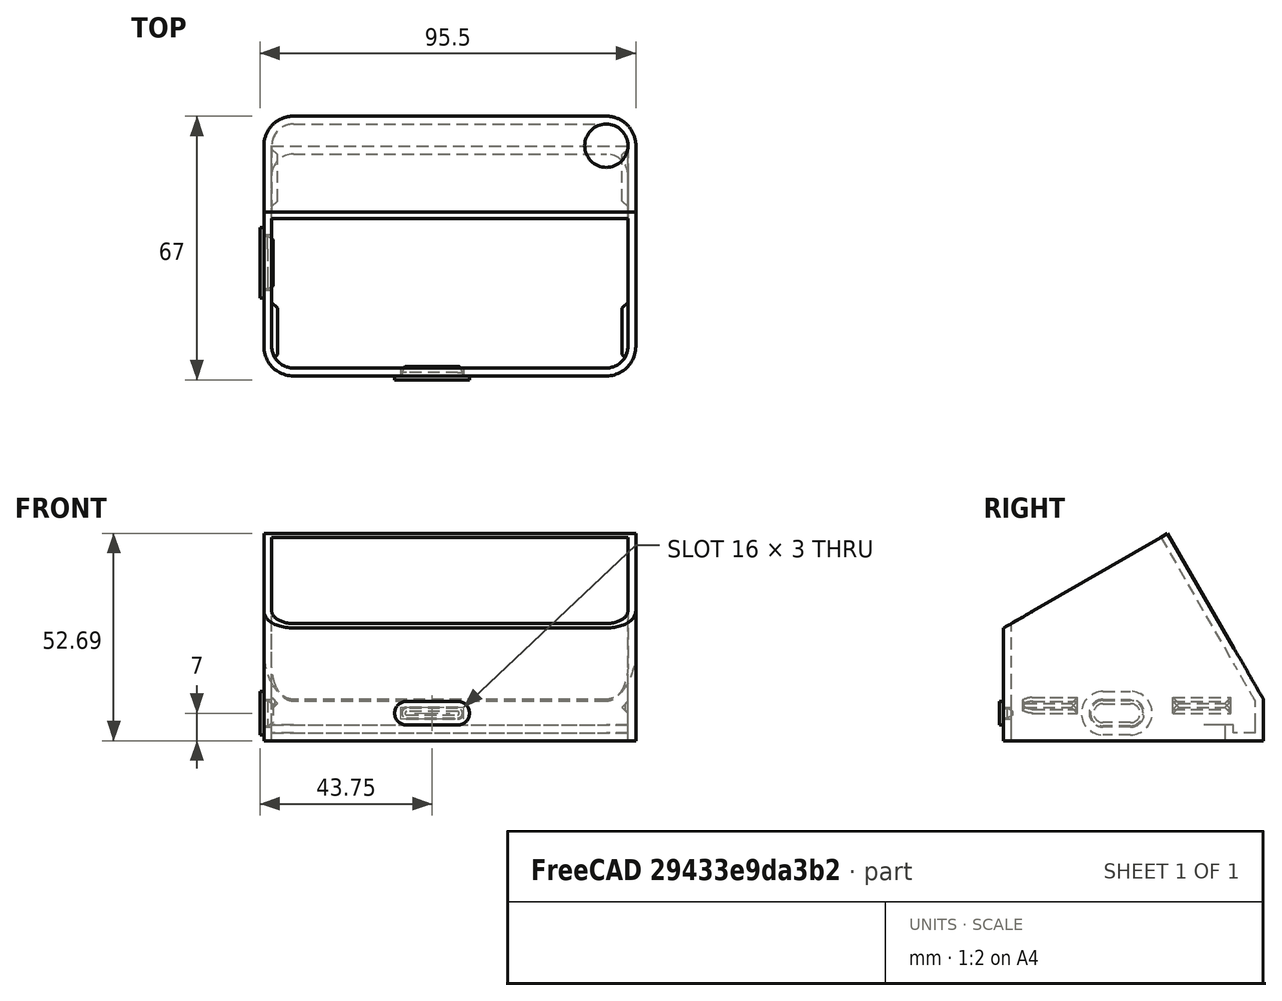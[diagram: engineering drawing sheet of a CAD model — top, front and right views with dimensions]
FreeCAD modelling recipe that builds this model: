
FCSTD DOCUMENT  (FreeCAD 0.21R33771 (Git))
Label: 2432S028
License: All rights reserved
LicenseURL: http://en.wikipedia.org/wiki/All_rights_reserved
objects: Sketcher::SketchObject×12, Part::Extrusion×11, Part::Box×7, Part::Chamfer×6, Part::Cut×4, Part::FeaturePython×3, Mesh::Feature×3, Part::MultiCommon×1, Part::MultiFuse×1
note: 45 computed .brp shape members not serialized (recipe doc carries the construction recipe); baked Part::Feature solids carry a one-line shape summary decoded from their .brp

FEATURE [Sketcher::SketchObject] Sketch  label="Basis"
  FullyConstrained = true
  sketch-geometry (22):
    g0: LineSegment StartX=-39.75 StartY=33 StartZ=0 EndX=39.75 EndY=33 EndZ=0
    g1: LineSegment StartX=47.25 StartY=25.5 StartZ=0 EndX=47.25 EndY=-25.5 EndZ=0
    g2: LineSegment StartX=39.75 StartY=-33 StartZ=0 EndX=-39.75 EndY=-33 EndZ=0
    g3: LineSegment StartX=-47.25 StartY=-25.5 StartZ=0 EndX=-47.25 EndY=25.5 EndZ=0
    g4: ArcOfCircle CenterX=-39.75 CenterY=25.5 CenterZ=0 NormalX=0 NormalY=0 NormalZ=1 AngleXU=0 Radius=7.5 StartAngle=1.5708 EndAngle=3.14159
    g5: GeomPoint X=-47.25 Y=33 Z=0
    g6: ArcOfCircle CenterX=39.75 CenterY=25.5 CenterZ=0 NormalX=0 NormalY=0 NormalZ=1 AngleXU=0 Radius=7.5 StartAngle=0 EndAngle=1.5708
    g7: GeomPoint X=47.25 Y=33 Z=0
    g8: ArcOfCircle CenterX=39.75 CenterY=-25.5 CenterZ=0 NormalX=0 NormalY=0 NormalZ=1 AngleXU=0 Radius=7.5 StartAngle=4.71239 EndAngle=6.28319
    g9: GeomPoint X=47.25 Y=-33 Z=0
    g10: ArcOfCircle CenterX=-39.75 CenterY=-25.5 CenterZ=0 NormalX=0 NormalY=0 NormalZ=1 AngleXU=0 Radius=7.5 StartAngle=3.14159 EndAngle=4.71239
    g11: GeomPoint X=-47.25 Y=-33 Z=0
    g12: ArcOfCircle CenterX=39.75 CenterY=17.9 CenterZ=0 NormalX=0 NormalY=0 NormalZ=1 AngleXU=0 Radius=5.5 StartAngle=4e-16 EndAngle=1.5708
    g13: LineSegment StartX=45.25 StartY=17.9 StartZ=0 EndX=45.25 EndY=-25.5 EndZ=0
    g14: ArcOfCircle CenterX=39.75 CenterY=-25.5 CenterZ=0 NormalX=0 NormalY=0 NormalZ=1 AngleXU=0 Radius=5.5 StartAngle=4.71239 EndAngle=6.28319
    g15: LineSegment StartX=39.75 StartY=-31 StartZ=0 EndX=-39.75 EndY=-31 EndZ=0
    g16: ArcOfCircle CenterX=-39.75 CenterY=-25.5 CenterZ=0 NormalX=0 NormalY=0 NormalZ=1 AngleXU=0 Radius=5.5 StartAngle=3.14159 EndAngle=4.71239
    g17: LineSegment StartX=-45.25 StartY=-25.5 StartZ=0 EndX=-45.25 EndY=17.9 EndZ=0
    g18: ArcOfCircle CenterX=-39.75 CenterY=17.9 CenterZ=0 NormalX=0 NormalY=0 NormalZ=1 AngleXU=0 Radius=5.5 StartAngle=1.5708 EndAngle=3.14159
    g19: LineSegment StartX=-39.75 StartY=23.4 StartZ=0 EndX=39.75 EndY=23.4 EndZ=0
    g20: GeomPoint X=45.25 Y=23.4 Z=0
    g21: GeomPoint X=-45.25 Y=-31 Z=0
  constraints (50):
    c: Horizontal(g0)
    c: Horizontal(g2)
    c: Vertical(g1)
    c: Vertical(g3)
    c: DistanceY(g9,g7) = 66
    c: Symmetric(g5,g9,g-1)
    c: PointOnObject(g5,g0)
    c: PointOnObject(g5,g3)
    c: Tangent(g0,g4) = 1.5708
    c: Tangent(g3,g4) = 1.5708
    c: PointOnObject(g7,g0)
    c: PointOnObject(g7,g1)
    c: Tangent(g0,g6) = 1.5708
    c: Tangent(g1,g6) = 1.5708
    c: PointOnObject(g9,g1)
    c: PointOnObject(g9,g2)
    c: Tangent(g1,g8) = 1.5708
    c: Tangent(g2,g8) = 1.5708
    c: PointOnObject(g11,g2)
    c: PointOnObject(g11,g3)
    c: Tangent(g2,g10) = 1.5708
    c: Tangent(g3,g10) = 1.5708
    c: Equal(g8,g10)
    c: Equal(g10,g4)
    c: Equal(g4,g6)
    c: Tangent(g12,g13) = 1.5708
    c: Tangent(g13,g14) = 1.5708
    c: Tangent(g14,g15) = 1.5708
    c: Tangent(g15,g16) = 1.5708
    c: Tangent(g16,g17) = 1.5708
    c: Tangent(g17,g18) = 1.5708
    c: Tangent(g18,g19) = 1.5708
    c: Tangent(g19,g12) = 1.5708
    c: Horizontal(g15)
    c: Vertical(g13)
    c: Vertical(g17)
    c: Equal(g12,g14)
    c: Equal(g14,g16)
    c: Equal(g16,g18)
    c: PointOnObject(g20,g13)
    c: PointOnObject(g20,g19)
    c: PointOnObject(g21,g15)
    c: PointOnObject(g21,g17)
    c: DistanceY(g14,g12) = 54.4
    c: DistanceX(g17,g12) = 90.5
    c: Diameter(g12) = 11
    c: Symmetric(g12,g17,g-2)
    c: DistanceY(g2,g14) = 2
    c: Coincident(g10,g16)
    c: DistanceY(g18,g4) = 2.1
FEATURE [Part::Box] Box  label="Cube"
  AttacherType = Attacher::AttachEngine3D
  Height = 100
  Length = 100
  Placement = pos=(-50,39.3072,-0.4) rot=(1,0,0;0.523599rad)
  Width = 100
FEATURE [Sketcher::SketchObject] Sketch001
  ExternalGeometry = -> [Sketch]
  FullyConstrained = true
  sketch-geometry (20):
    g0: ArcOfCircle CenterX=-39.75 CenterY=25.5 CenterZ=0 NormalX=0 NormalY=0 NormalZ=1 AngleXU=0 Radius=7.5 StartAngle=1.5708 EndAngle=3.14159
    g1: LineSegment StartX=-39.75 StartY=33 StartZ=0 EndX=39.75 EndY=33 EndZ=0
    g2: ArcOfCircle CenterX=39.75 CenterY=25.5 CenterZ=0 NormalX=0 NormalY=0 NormalZ=1 AngleXU=0 Radius=7.5 StartAngle=1e-16 EndAngle=1.5708
    g3: LineSegment StartX=47.25 StartY=25.5 StartZ=0 EndX=47.25 EndY=-25.5 EndZ=0
    g4: ArcOfCircle CenterX=39.75 CenterY=-25.5 CenterZ=0 NormalX=0 NormalY=0 NormalZ=1 AngleXU=0 Radius=7.5 StartAngle=4.71239 EndAngle=6.28319
    g5: LineSegment StartX=39.75 StartY=-33 StartZ=0 EndX=-39.75 EndY=-33 EndZ=0
    g6: ArcOfCircle CenterX=-39.75 CenterY=-25.5 CenterZ=0 NormalX=0 NormalY=0 NormalZ=1 AngleXU=0 Radius=7.5 StartAngle=3.14159 EndAngle=4.71239
    g7: LineSegment StartX=-47.25 StartY=-25.5 StartZ=0 EndX=-47.25 EndY=25.5 EndZ=0
    g8: GeomPoint X=-47.25 Y=33 Z=0
    g9: GeomPoint X=47.25 Y=-33 Z=0
    g10: ArcOfCircle CenterX=-39.75 CenterY=17.9 CenterZ=0 NormalX=0 NormalY=0 NormalZ=1 AngleXU=0 Radius=5.5 StartAngle=1.5708 EndAngle=3.14159
    g11: LineSegment StartX=-39.75 StartY=23.4 StartZ=0 EndX=39.75 EndY=23.4 EndZ=0
    g12: ArcOfCircle CenterX=39.75 CenterY=17.9 CenterZ=0 NormalX=0 NormalY=0 NormalZ=1 AngleXU=0 Radius=5.5 StartAngle=0 EndAngle=1.5708
    g13: LineSegment StartX=45.25 StartY=17.9 StartZ=0 EndX=45.25 EndY=-25.5 EndZ=0
    g14: ArcOfCircle CenterX=39.75 CenterY=-25.5 CenterZ=0 NormalX=0 NormalY=0 NormalZ=1 AngleXU=0 Radius=5.5 StartAngle=4.71239 EndAngle=6.28319
    g15: LineSegment StartX=39.75 StartY=-31 StartZ=0 EndX=-39.75 EndY=-31 EndZ=0
    g16: ArcOfCircle CenterX=-39.75 CenterY=-25.5 CenterZ=0 NormalX=0 NormalY=0 NormalZ=1 AngleXU=0 Radius=5.5 StartAngle=3.14159 EndAngle=4.71239
    g17: LineSegment StartX=-45.25 StartY=-25.5 StartZ=0 EndX=-45.25 EndY=17.9 EndZ=0
    g18: GeomPoint X=-45.25 Y=23.4 Z=0
    g19: GeomPoint X=45.25 Y=-31 Z=0
  constraints (44):
    c: Tangent(g0,g1) = 1.5708
    c: Tangent(g1,g2) = 1.5708
    c: Tangent(g2,g3) = 1.5708
    c: Tangent(g3,g4) = 1.5708
    c: Tangent(g4,g5) = 1.5708
    c: Tangent(g5,g6) = 1.5708
    c: Tangent(g6,g7) = 1.5708
    c: Tangent(g7,g0) = 1.5708
    c: Horizontal(g1)
    c: Horizontal(g5)
    c: Vertical(g3)
    c: Vertical(g7)
    c: Equal(g0,g2)
    c: Equal(g2,g4)
    c: Equal(g4,g6)
    c: PointOnObject(g8,g1)
    c: PointOnObject(g8,g7)
    c: PointOnObject(g9,g3)
    c: PointOnObject(g9,g5)
    c: Coincident(g-6,g4)
    c: Coincident(g0,g-3)
    c: Horizontal(g-3,g0)
    c: Tangent(g10,g11) = 1.5708
    c: Tangent(g11,g12) = 1.5708
    c: Tangent(g12,g13) = 1.5708
    c: Tangent(g13,g14) = 1.5708
    c: Tangent(g14,g15) = 1.5708
    c: Tangent(g15,g16) = 1.5708
    c: Tangent(g16,g17) = 1.5708
    c: Tangent(g17,g10) = 1.5708
    c: Horizontal(g11)
    c: Horizontal(g15)
    c: Vertical(g13)
    c: Vertical(g17)
    c: Equal(g10,g12)
    c: Equal(g12,g14)
    c: Equal(g14,g16)
    c: PointOnObject(g18,g11)
    c: PointOnObject(g18,g17)
    c: PointOnObject(g19,g13)
    c: PointOnObject(g19,g15)
    c: Coincident(g14,g4)
    c: Coincident(g10,g-5)
    c: Horizontal(g-5,g10)
FEATURE [Part::Extrusion] Extrude
  Base = -> Sketch001
  Dir = (0,0,1)
  DirMode = 2
  FaceMakerClass = Part::FaceMakerBullseye
  LengthFwd = 2
  LengthRev = 0
  Solid = true
  Symmetric = false
FEATURE [Sketcher::SketchObject] Sketch002
  ExternalGeometry = -> [Sketch]
  FullyConstrained = true
  Placement = pos=(0,0,2) rot=(0,0,1;0rad)
  sketch-geometry (26):
    g0: ArcOfCircle CenterX=-39.75 CenterY=25.5 CenterZ=0 NormalX=0 NormalY=0 NormalZ=1 AngleXU=0 Radius=7.5 StartAngle=1.5708 EndAngle=3.14159
    g1: LineSegment StartX=-39.75 StartY=33 StartZ=0 EndX=39.75 EndY=33 EndZ=0
    g2: ArcOfCircle CenterX=39.75 CenterY=25.5 CenterZ=0 NormalX=0 NormalY=0 NormalZ=1 AngleXU=0 Radius=7.5 StartAngle=4e-16 EndAngle=1.5708
    g3: LineSegment StartX=47.25 StartY=25.5 StartZ=0 EndX=47.25 EndY=-25.5 EndZ=0
    g4: ArcOfCircle CenterX=39.75 CenterY=-25.5 CenterZ=0 NormalX=0 NormalY=0 NormalZ=1 AngleXU=0 Radius=7.5 StartAngle=4.71239 EndAngle=6.28319
    g5: LineSegment StartX=39.75 StartY=-33 StartZ=0 EndX=-39.75 EndY=-33 EndZ=0
    g6: ArcOfCircle CenterX=-39.75 CenterY=-25.5 CenterZ=0 NormalX=0 NormalY=0 NormalZ=1 AngleXU=0 Radius=7.5 StartAngle=3.14159 EndAngle=4.71239
    g7: LineSegment StartX=-47.25 StartY=-25.5 StartZ=0 EndX=-47.25 EndY=25.5 EndZ=0
    g8: GeomPoint X=-47.25 Y=33 Z=0
    g9: GeomPoint X=47.25 Y=-33 Z=0
    g10: ArcOfCircle CenterX=-39.75 CenterY=17.9 CenterZ=0 NormalX=0 NormalY=0 NormalZ=1 AngleXU=0 Radius=5.5 StartAngle=1.5708 EndAngle=3.14159
    g11: LineSegment StartX=-39.75 StartY=23.4 StartZ=0 EndX=39.75 EndY=23.4 EndZ=0
    g12: ArcOfCircle CenterX=39.75 CenterY=17.9 CenterZ=0 NormalX=0 NormalY=0 NormalZ=1 AngleXU=0 Radius=5.5 StartAngle=0 EndAngle=1.5708
    g13: LineSegment StartX=45.25 StartY=17.9 StartZ=0 EndX=45.25 EndY=-25.5 EndZ=0
    g14: ArcOfCircle CenterX=39.75 CenterY=-25.5 CenterZ=0 NormalX=0 NormalY=0 NormalZ=1 AngleXU=0 Radius=5.5 StartAngle=4.71239 EndAngle=6.28319
    g15: LineSegment StartX=39.75 StartY=-31 StartZ=0 EndX=-39.75 EndY=-31 EndZ=0
    g16: ArcOfCircle CenterX=-39.75 CenterY=-25.5 CenterZ=0 NormalX=0 NormalY=0 NormalZ=1 AngleXU=0 Radius=5.5 StartAngle=3.14159 EndAngle=4.71239
    g17: LineSegment StartX=-45.25 StartY=-25.5 StartZ=0 EndX=-45.25 EndY=17.9 EndZ=0
    g18: GeomPoint X=-45.25 Y=23.4 Z=0
    g19: GeomPoint X=45.25 Y=-31 Z=0
    g20: ArcOfCircle CenterX=-39.75 CenterY=25.5 CenterZ=0 NormalX=0 NormalY=0 NormalZ=1 AngleXU=0 Radius=5.5 StartAngle=1.5708 EndAngle=3.14159
    g21: LineSegment StartX=-39.75 StartY=31 StartZ=0 EndX=39.75 EndY=31 EndZ=0
    g22: ArcOfCircle CenterX=39.75 CenterY=25.5 CenterZ=0 NormalX=0 NormalY=0 NormalZ=1 AngleXU=0 Radius=5.5 StartAngle=0 EndAngle=1.5708
    g23: LineSegment StartX=-45.25 StartY=25.4 StartZ=0 EndX=45.25 EndY=25.4 EndZ=0
    g24: LineSegment StartX=-45.25 StartY=25.5 StartZ=0 EndX=-45.25 EndY=25.4 EndZ=0
    g25: LineSegment StartX=45.25 StartY=25.5 StartZ=0 EndX=45.25 EndY=25.4 EndZ=0
  constraints (62):
    c: Tangent(g0,g1) = 1.5708
    c: Tangent(g1,g2) = 1.5708
    c: Tangent(g2,g3) = 1.5708
    c: Tangent(g3,g4) = 1.5708
    c: Tangent(g4,g5) = 1.5708
    c: Tangent(g5,g6) = 1.5708
    c: Tangent(g6,g7) = 1.5708
    c: Tangent(g7,g0) = 1.5708
    c: Horizontal(g1)
    c: Horizontal(g5)
    c: Vertical(g3)
    c: Vertical(g7)
    c: Equal(g0,g2)
    c: Equal(g2,g4)
    c: Equal(g4,g6)
    c: PointOnObject(g8,g1)
    c: PointOnObject(g8,g7)
    c: PointOnObject(g9,g3)
    c: PointOnObject(g9,g5)
    c: Coincident(g4,g-6)
    c: Coincident(g0,g-3)
    c: Horizontal(g-3,g0)
    c: Tangent(g10,g11) = 1.5708
    c: Tangent(g11,g12) = 1.5708
    c: Tangent(g12,g13) = 1.5708
    c: Tangent(g13,g14) = 1.5708
    c: Tangent(g14,g15) = 1.5708
    c: Tangent(g15,g16) = 1.5708
    c: Tangent(g16,g17) = 1.5708
    c: Tangent(g17,g10) = 1.5708
    c: Horizontal(g11)
    c: Horizontal(g15)
    c: Vertical(g13)
    c: Vertical(g17)
    c: Equal(g10,g12)
    c: Equal(g12,g14)
    c: Equal(g14,g16)
    c: PointOnObject(g18,g11)
    c: PointOnObject(g18,g17)
    c: PointOnObject(g19,g13)
    c: PointOnObject(g19,g15)
    c: Coincident(g4,g14)
    c: Coincident(g10,g-5)
    c: Horizontal(g14,g-6)
    c: Coincident(g20,g0)
    c: Vertical(g0,g20)
    c: Horizontal(g0,g20)
    c: DistanceY(g20,g0) = 2
    c: Coincident(g21,g20)
    c: Horizontal(g21)
    c: Coincident(g22,g2)
    c: Coincident(g22,g21)
    c: Equal(g22,g20)
    c: Horizontal(g2,g22)
    c: Horizontal(g23)
    c: Coincident(g24,g20)
    c: Coincident(g24,g23)
    c: Vertical(g24)
    c: Coincident(g25,g22)
    c: Coincident(g25,g23)
    c: Vertical(g25)
    c: DistanceY(g10,g23) = 2
FEATURE [Part::Extrusion] Extrude001  label="Extrude_2mm"
  Base = -> Sketch002
  Dir = (0,0,1)
  DirMode = 2
  FaceMakerClass = Part::FaceMakerBullseye
  LengthFwd = 2
  LengthRev = 0
  Solid = true
  Symmetric = false
FEATURE [Sketcher::SketchObject] Sketch003
  ExternalGeometry = -> [Sketch]
  FullyConstrained = true
  Placement = pos=(0,0,4) rot=(0,0,1;0rad)
  sketch-geometry (20):
    g0: ArcOfCircle CenterX=-39.75 CenterY=25.5 CenterZ=0 NormalX=0 NormalY=0 NormalZ=1 AngleXU=0 Radius=7.5 StartAngle=1.5708 EndAngle=3.14159
    g1: LineSegment StartX=-39.75 StartY=33 StartZ=0 EndX=39.75 EndY=33 EndZ=0
    g2: ArcOfCircle CenterX=39.75 CenterY=25.5 CenterZ=0 NormalX=0 NormalY=0 NormalZ=1 AngleXU=0 Radius=7.5 StartAngle=0 EndAngle=1.5708
    g3: LineSegment StartX=47.25 StartY=25.5 StartZ=0 EndX=47.25 EndY=-25.5 EndZ=0
    g4: ArcOfCircle CenterX=39.75 CenterY=-25.5 CenterZ=0 NormalX=0 NormalY=0 NormalZ=1 AngleXU=0 Radius=7.5 StartAngle=4.71239 EndAngle=6.28319
    g5: LineSegment StartX=39.75 StartY=-33 StartZ=0 EndX=-39.75 EndY=-33 EndZ=0
    g6: ArcOfCircle CenterX=-39.75 CenterY=-25.5 CenterZ=0 NormalX=0 NormalY=0 NormalZ=1 AngleXU=0 Radius=7.5 StartAngle=3.14159 EndAngle=4.71239
    g7: LineSegment StartX=-47.25 StartY=-25.5 StartZ=0 EndX=-47.25 EndY=25.5 EndZ=0
    g8: GeomPoint X=-47.25 Y=33 Z=0
    g9: GeomPoint X=47.25 Y=-33 Z=0
    g10: ArcOfCircle CenterX=-39.75 CenterY=25.5 CenterZ=0 NormalX=0 NormalY=0 NormalZ=1 AngleXU=0 Radius=5.5 StartAngle=1.5708 EndAngle=3.14159
    g11: LineSegment StartX=-39.75 StartY=31 StartZ=0 EndX=39.75 EndY=31 EndZ=0
    g12: ArcOfCircle CenterX=39.75 CenterY=25.5 CenterZ=0 NormalX=0 NormalY=0 NormalZ=1 AngleXU=0 Radius=5.5 StartAngle=0 EndAngle=1.5708
    g13: LineSegment StartX=45.25 StartY=25.5 StartZ=0 EndX=45.25 EndY=-25.5 EndZ=0
    g14: ArcOfCircle CenterX=39.75 CenterY=-25.5 CenterZ=0 NormalX=0 NormalY=0 NormalZ=1 AngleXU=0 Radius=5.5 StartAngle=4.71239 EndAngle=6.28319
    g15: LineSegment StartX=39.75 StartY=-31 StartZ=0 EndX=-39.75 EndY=-31 EndZ=0
    g16: ArcOfCircle CenterX=-39.75 CenterY=-25.5 CenterZ=0 NormalX=0 NormalY=0 NormalZ=1 AngleXU=0 Radius=5.5 StartAngle=3.14159 EndAngle=4.71239
    g17: LineSegment StartX=-45.25 StartY=-25.5 StartZ=0 EndX=-45.25 EndY=25.5 EndZ=0
    g18: GeomPoint X=-45.25 Y=31 Z=0
    g19: GeomPoint X=45.25 Y=-31 Z=0
  constraints (45):
    c: Tangent(g0,g1) = 1.5708
    c: Tangent(g1,g2) = 1.5708
    c: Tangent(g2,g3) = 1.5708
    c: Tangent(g3,g4) = 1.5708
    c: Tangent(g4,g5) = 1.5708
    c: Tangent(g5,g6) = 1.5708
    c: Tangent(g6,g7) = 1.5708
    c: Tangent(g7,g0) = 1.5708
    c: Horizontal(g1)
    c: Horizontal(g5)
    c: Vertical(g3)
    c: Vertical(g7)
    c: Equal(g0,g2)
    c: Equal(g2,g4)
    c: Equal(g4,g6)
    c: PointOnObject(g8,g1)
    c: PointOnObject(g8,g7)
    c: PointOnObject(g9,g3)
    c: PointOnObject(g9,g5)
    c: Coincident(g-5,g4)
    c: Coincident(g0,g-3)
    c: Horizontal(g-3,g0)
    c: Tangent(g10,g11) = 1.5708
    c: Tangent(g12,g13) = 1.5708
    c: Tangent(g13,g14) = 1.5708
    c: Tangent(g14,g15) = 1.5708
    c: Tangent(g15,g16) = 1.5708
    c: Tangent(g16,g17) = 1.5708
    c: Tangent(g17,g10) = 1.5708
    c: Horizontal(g11)
    c: Horizontal(g15)
    c: Vertical(g13)
    c: Vertical(g17)
    c: Equal(g10,g12)
    c: Equal(g12,g14)
    c: Equal(g14,g16)
    c: PointOnObject(g18,g11)
    c: PointOnObject(g18,g17)
    c: PointOnObject(g19,g13)
    c: PointOnObject(g19,g15)
    c: Coincident(g14,g4)
    c: Coincident(g11,g12)
    c: Coincident(g0,g10)
    c: Horizontal(g15,g-6)
    c: Vertical(g12,g11)
FEATURE [Part::Extrusion] Extrude002  label="Extrude_4mm"
  Base = -> Sketch003
  Dir = (0,0,1)
  DirMode = 2
  FaceMakerClass = Part::FaceMakerBullseye
  LengthFwd = 10
  LengthRev = 0
  Solid = true
  Symmetric = false
FEATURE [Part::Extrusion] Extrude003  label="Extrude_6mm"
  Base = -> Sketch003
  Dir = (0,0,1)
  DirMode = 2
  FaceMakerClass = Part::FaceMakerBullseye
  LengthFwd = 52
  LengthRev = 0
  Solid = true
  Symmetric = false
FEATURE [Part::Box] Box001  label="Cube001"
  AttacherType = Attacher::AttachEngine3D
  Height = 100
  Length = 100
  Placement = pos=(-50,-49.5397,19.0874) rot=(1,0,0;0.523599rad)
  Width = 100
FEATURE [Part::Box] Box002  label="Cube002"
  AttacherType = Attacher::AttachEngine3D
  Height = 100
  Length = 100
  Placement = pos=(-50,37.5751,-1.4) rot=(1,0,0;0.523599rad)
  Width = 2
FEATURE [Sketcher::SketchObject] Sketch004
  ExternalGeometry = -> [Sketch]
  FullyConstrained = false
  sketch-geometry (12):
    g0: ArcOfCircle CenterX=-39.75 CenterY=25.5 CenterZ=0 NormalX=0 NormalY=0 NormalZ=1 AngleXU=0 Radius=7.5 StartAngle=1.5708 EndAngle=3.14159
    g1: LineSegment StartX=-39.75 StartY=33 StartZ=0 EndX=39.75 EndY=33 EndZ=0
    g2: ArcOfCircle CenterX=39.75 CenterY=25.5 CenterZ=0 NormalX=0 NormalY=0 NormalZ=1 AngleXU=0 Radius=7.5 StartAngle=1e-16 EndAngle=1.5708
    g3: LineSegment StartX=47.25 StartY=25.5 StartZ=0 EndX=47.25 EndY=-25.5 EndZ=0
    g4: ArcOfCircle CenterX=39.75 CenterY=-25.5 CenterZ=0 NormalX=0 NormalY=0 NormalZ=1 AngleXU=0 Radius=7.5 StartAngle=4.71239 EndAngle=6.28319
    g5: LineSegment StartX=39.75 StartY=-33 StartZ=0 EndX=-39.75 EndY=-33 EndZ=0
    g6: ArcOfCircle CenterX=-39.75 CenterY=-25.5 CenterZ=0 NormalX=0 NormalY=0 NormalZ=1 AngleXU=0 Radius=7.5 StartAngle=3.14159 EndAngle=4.71239
    g7: LineSegment StartX=-47.25 StartY=-25.5 StartZ=0 EndX=-47.25 EndY=25.5 EndZ=0
    g8: GeomPoint X=-47.25 Y=33 Z=0
    g9: GeomPoint X=47.25 Y=-33 Z=0
    g10: GeomPoint X=-22 Y=14 Z=0
    g11: GeomPoint X=22 Y=-30 Z=0
  constraints (22):
    c: Tangent(g0,g1) = 1.5708
    c: Tangent(g1,g2) = 1.5708
    c: Tangent(g2,g3) = 1.5708
    c: Tangent(g3,g4) = 1.5708
    c: Tangent(g4,g5) = 1.5708
    c: Tangent(g5,g6) = 1.5708
    c: Tangent(g6,g7) = 1.5708
    c: Tangent(g7,g0) = 1.5708
    c: Horizontal(g1)
    c: Horizontal(g5)
    c: Vertical(g3)
    c: Vertical(g7)
    c: Equal(g0,g2)
    c: Equal(g2,g4)
    c: Equal(g4,g6)
    c: PointOnObject(g8,g1)
    c: PointOnObject(g8,g7)
    c: PointOnObject(g9,g3)
    c: PointOnObject(g9,g5)
    c: Coincident(g0,g-3)
    c: Horizontal(g-3,g0)
    c: Coincident(g4,g-4)
FEATURE [Part::Extrusion] Extrude004
  Base = -> Sketch004
  Dir = (0,0,1)
  DirMode = 2
  FaceMakerClass = Part::FaceMakerBullseye
  LengthFwd = 56
  LengthRev = 0
  Solid = true
  Symmetric = false
FEATURE [Part::MultiCommon] Common
  Shapes = -> [Box002,Extrude004]
FEATURE [Part::MultiFuse] Fusion
  Shapes = -> [Common,Extrude,Extrude001,Extrude002,Extrude003]
FEATURE [Part::Cut] Cut
  Base = -> Fusion
  Tool = -> Box
FEATURE [Part::Cut] Cut001
  Base = -> Cut
  Tool = -> Box001
FEATURE [Part::Box] Box003  label="Cube003"
  AttacherType = Attacher::AttachEngine3D
  Height = 3
  Length = 1.5
  Placement = pos=(43.75,-29,7) rot=(0,0,1;0rad)
  Width = 14.7
FEATURE [Part::Chamfer] Chamfer
  Base = -> Box003
  Edges = 4 edges r=1.49: [Edge1,Edge2,Edge3,Edge4]
FEATURE [Part::Box] Box004  label="Cube004"
  AttacherType = Attacher::AttachEngine3D
  Height = 3
  Length = 1.5
  Placement = pos=(-45.25,-29,8) rot=(0,0,1;0rad)
  Width = 14.7
FEATURE [Part::Chamfer] Chamfer001
  Base = -> Box004
  Edges = 4 edges r=1.49: [Edge5,Edge6,Edge7,Edge8]
FEATURE [Sketcher::SketchObject] Sketch005  label="Basis001_bEZEL"
  FullyConstrained = true
  Placement = pos=(0,-2.75,0) rot=(0,1,0;3.14159rad)
  sketch-geometry (46):
    g0: ArcOfCircle CenterX=40 CenterY=22 CenterZ=0 NormalX=0 NormalY=0 NormalZ=1 AngleXU=0 Radius=3 StartAngle=4e-16 EndAngle=1.5708
    g1: LineSegment StartX=43 StartY=22 StartZ=0 EndX=43 EndY=-22 EndZ=0
    g2: ArcOfCircle CenterX=40 CenterY=-22 CenterZ=0 NormalX=0 NormalY=0 NormalZ=1 AngleXU=0 Radius=3 StartAngle=4.71239 EndAngle=6.28319
    g3: LineSegment StartX=40 StartY=-25 StartZ=0 EndX=-40 EndY=-25 EndZ=0
    g4: ArcOfCircle CenterX=-40 CenterY=-22 CenterZ=0 NormalX=0 NormalY=0 NormalZ=1 AngleXU=0 Radius=3 StartAngle=3.14159 EndAngle=4.71239
    g5: LineSegment StartX=-43 StartY=-22 StartZ=0 EndX=-43 EndY=22 EndZ=0
    g6: ArcOfCircle CenterX=-40 CenterY=22 CenterZ=0 NormalX=0 NormalY=0 NormalZ=1 AngleXU=0 Radius=3 StartAngle=1.5708 EndAngle=3.14159
    g7: LineSegment StartX=-40 StartY=25 StartZ=0 EndX=40 EndY=25 EndZ=0
    g8: GeomPoint X=43 Y=25 Z=0
    g9: GeomPoint X=-43 Y=-25 Z=0
    g10: Circle CenterX=-39 CenterY=21 CenterZ=0 NormalX=0 NormalY=0 NormalZ=1 AngleXU=0 Radius=1.6
    g11: Circle CenterX=-39 CenterY=-21 CenterZ=0 NormalX=0 NormalY=0 NormalZ=1 AngleXU=0 Radius=1.6
    g12: Circle CenterX=39 CenterY=21 CenterZ=0 NormalX=0 NormalY=0 NormalZ=1 AngleXU=0 Radius=1.6
    g13: Circle CenterX=39 CenterY=-21 CenterZ=0 NormalX=0 NormalY=0 NormalZ=1 AngleXU=0 Radius=1.6
    g14: LineSegment StartX=-35 StartY=25 StartZ=0 EndX=36 EndY=25 EndZ=0
    g15: LineSegment StartX=36 StartY=25 StartZ=0 EndX=36 EndY=-25 EndZ=0
    g16: LineSegment StartX=36 StartY=-25 StartZ=0 EndX=-35 EndY=-25 EndZ=0
    g17: LineSegment StartX=-35 StartY=-25 StartZ=0 EndX=-35 EndY=25 EndZ=0
    g18: LineSegment StartX=-40.4 StartY=-12 StartZ=0 EndX=-37.4 EndY=-12 EndZ=0
    g19: LineSegment StartX=-37.4 StartY=-12 StartZ=0 EndX=-37.4 EndY=-17 EndZ=0
    g20: LineSegment StartX=-37.4 StartY=-17 StartZ=0 EndX=-40.4 EndY=-17 EndZ=0
    g21: LineSegment StartX=-40.4 StartY=-17 StartZ=0 EndX=-40.4 EndY=-12 EndZ=0
    g22: LineSegment StartX=-2 StartY=-25 StartZ=0 EndX=11 EndY=-25 EndZ=0
    g23: LineSegment StartX=11 StartY=-25 StartZ=0 EndX=11 EndY=-28 EndZ=0
    g24: LineSegment StartX=11 StartY=-28 StartZ=0 EndX=-2 EndY=-28 EndZ=0
    g25: LineSegment StartX=-2 StartY=-28 StartZ=0 EndX=-2 EndY=-25 EndZ=0
    g26: LineSegment StartX=43 StartY=3 StartZ=0 EndX=53 EndY=3 EndZ=0
    g27: LineSegment StartX=53 StartY=3 StartZ=0 EndX=53 EndY=-6 EndZ=0
    g28: LineSegment StartX=53 StartY=-6 StartZ=0 EndX=43 EndY=-6 EndZ=0
    g29: LineSegment StartX=43 StartY=-6 StartZ=0 EndX=43 EndY=3 EndZ=0
    g30: LineSegment StartX=43 StartY=14 StartZ=0 EndX=45 EndY=14 EndZ=0
    g31: LineSegment StartX=45 StartY=14 StartZ=0 EndX=45 EndY=6 EndZ=0
    g32: LineSegment StartX=45 StartY=6 StartZ=0 EndX=43 EndY=6 EndZ=0
    g33: LineSegment StartX=43 StartY=6 StartZ=0 EndX=43 EndY=14 EndZ=0
    g34: LineSegment StartX=-31.5 StartY=-25 StartZ=0 EndX=-23.5 EndY=-25 EndZ=0
    g35: LineSegment StartX=-23.5 StartY=-25 StartZ=0 EndX=-23.5 EndY=-27 EndZ=0
    g36: LineSegment StartX=-23.5 StartY=-27 StartZ=0 EndX=-31.5 EndY=-27 EndZ=0
    g37: LineSegment StartX=-31.5 StartY=-27 StartZ=0 EndX=-31.5 EndY=-25 EndZ=0
    g38: LineSegment StartX=-16.5 StartY=-25 StartZ=0 EndX=-8.5 EndY=-25 EndZ=0
    g39: LineSegment StartX=-8.5 StartY=-25 StartZ=0 EndX=-8.5 EndY=-27 EndZ=0
    g40: LineSegment StartX=-8.5 StartY=-27 StartZ=0 EndX=-16.5 EndY=-27 EndZ=0
    g41: LineSegment StartX=-16.5 StartY=-27 StartZ=0 EndX=-16.5 EndY=-25 EndZ=0
    g42: LineSegment StartX=-33 StartY=22.5 StartZ=0 EndX=27 EndY=22.5 EndZ=0
    g43: LineSegment StartX=27 StartY=22.5 StartZ=0 EndX=27 EndY=-22.5 EndZ=0
    g44: LineSegment StartX=27 StartY=-22.5 StartZ=0 EndX=-33 EndY=-22.5 EndZ=0
    g45: LineSegment StartX=-33 StartY=-22.5 StartZ=0 EndX=-33 EndY=22.5 EndZ=0
  constraints (130):
    c: Tangent(g0,g1) = 1.5708
    c: Tangent(g1,g2) = 1.5708
    c: Tangent(g2,g3) = 1.5708
    c: Tangent(g3,g4) = 1.5708
    c: Tangent(g4,g5) = 1.5708
    c: Tangent(g5,g6) = 1.5708
    c: Tangent(g6,g7) = 1.5708
    c: Tangent(g7,g0) = 1.5708
    c: Horizontal(g3)
    c: Vertical(g1)
    c: Vertical(g5)
    c: Equal(g0,g2)
    c: Equal(g2,g4)
    c: Equal(g4,g6)
    c: PointOnObject(g8,g1)
    c: PointOnObject(g8,g7)
    c: PointOnObject(g9,g3)
    c: PointOnObject(g9,g5)
    c: DistanceY(g2,g0) = 50
    c: DistanceX(g5,g0) = 86
    c: Diameter(g0) = 6
    c: Symmetric(g6,g2,g-1)
    c: Horizontal(g7)
    c: Diameter(g10) = 3.2
    c: DistanceY(g10,g6) = 4
    c: DistanceX(g5,g10) = 4
    c: Equal(g10,g12)
    c: Horizontal(g10,g12)
    c: Vertical(g10,g11)
    c: Horizontal(g11,g13)
    c: Vertical(g13,g12)
    c: Equal(g10,g11)
    c: Equal(g11,g13)
    c: DistanceY(g2,g13) = 4
    c: DistanceX(g13,g1) = 4
    c: Coincident(g14,g15)
    c: Coincident(g15,g16)
    c: Coincident(g16,g17)
    c: Coincident(g17,g14)
    c: Horizontal(g14)
    c: Horizontal(g16)
    c: Vertical(g15)
    c: Vertical(g17)
    c: PointOnObject(g14,g7)
    c: PointOnObject(g16,g3)
    c: DistanceX(g14,g0) = 7
    c: DistanceX(g5,g14) = 8
    c: Coincident(g18,g19)
    c: Coincident(g19,g20)
    c: Coincident(g20,g21)
    c: Coincident(g21,g18)
    c: Horizontal(g18)
    c: Horizontal(g20)
    c: Vertical(g19)
    c: Vertical(g21)
    c: DistanceX(g20,g20) = 3
    c: DistanceY(g21,g21) = 5
    c: DistanceY(g3,g20) = 8
    c: DistanceX(g4,g20) = 2.6
    c: Coincident(g22,g23)
    c: Coincident(g23,g24)
    c: Coincident(g24,g25)
    c: Coincident(g25,g22)
    c: Horizontal(g22)
    c: Horizontal(g24)
    c: Vertical(g23)
    c: Vertical(g25)
    c: PointOnObject(g22,g3)
    c: DistanceX(g4,g22) = 41
    c: DistanceX(g22,g1) = 32
    c: DistanceY(g23,g23) = 3
    c: Coincident(g26,g27)
    c: Coincident(g27,g28)
    c: Coincident(g28,g29)
    c: Coincident(g29,g26)
    c: Horizontal(g26)
    c: Horizontal(g28)
    c: Vertical(g27)
    c: Vertical(g29)
    c: PointOnObject(g26,g1)
    c: DistanceY(g26,g0) = 22
    c: DistanceY(g2,g28) = 19
    c: DistanceX(g26,g26) = 10
    c: Coincident(g30,g31)
    c: Coincident(g31,g32)
    c: Coincident(g32,g33)
    c: Coincident(g33,g30)
    c: Horizontal(g30)
    c: Horizontal(g32)
    c: Vertical(g31)
    c: Vertical(g33)
    c: PointOnObject(g30,g1)
    c: DistanceY(g30,g0) = 11
    c: DistanceY(g2,g32) = 31
    c: DistanceX(g30,g30) = 2
    c: Coincident(g34,g35)
    c: Coincident(g35,g36)
    c: Coincident(g36,g37)
    c: Coincident(g37,g34)
    c: Horizontal(g34)
    c: Horizontal(g36)
    c: Vertical(g35)
    c: Vertical(g37)
    c: PointOnObject(g34,g3)
    c: Coincident(g38,g39)
    c: Coincident(g39,g40)
    c: Coincident(g40,g41)
    c: Coincident(g41,g38)
    c: Horizontal(g38)
    c: Horizontal(g40)
    c: Vertical(g39)
    c: Vertical(g41)
    c: PointOnObject(g38,g3)
    c: Equal(g31,g40)
    c: Equal(g40,g36)
    c: Equal(g32,g39)
    c: Equal(g39,g35)
    c: DistanceX(g4,g34) = 11.5
    c: DistanceX(g4,g38) = 26.5
    c: Coincident(g42,g43)
    c: Coincident(g43,g44)
    c: Coincident(g44,g45)
    c: Coincident(g45,g42)
    c: Horizontal(g42)
    c: Horizontal(g44)
    c: Vertical(g43)
    c: DistanceX(g44,g44) = 60
    c: DistanceY(g43,g43) = 45
    c: Symmetric(g42,g44,g-1)
    c: DistanceX(g14,g42) = 2
FEATURE [Sketcher::SketchObject] Sketch006
  ExternalGeometry = -> [Sketch005]
  FullyConstrained = true
  MapMode = 5
  Placement = pos=(0,-33,0) rot=(1,0,0;1.5708rad)
  Support = -> [Cut001]
  sketch-geometry (4):
    g0: ArcOfCircle CenterX=2 CenterY=7 CenterZ=0 NormalX=0 NormalY=0 NormalZ=1 AngleXU=0 Radius=1.5 StartAngle=4.71239 EndAngle=7.85398
    g1: ArcOfCircle CenterX=-11 CenterY=7 CenterZ=0 NormalX=0 NormalY=0 NormalZ=1 AngleXU=0 Radius=1.5 StartAngle=1.5708 EndAngle=4.71239
    g2: LineSegment StartX=2 StartY=8.5 StartZ=0 EndX=-11 EndY=8.5 EndZ=0
    g3: LineSegment StartX=-11 StartY=5.5 StartZ=0 EndX=2 EndY=5.5 EndZ=0
  constraints (10):
    c: Tangent(g0,g2) = -1.5708
    c: Tangent(g2,g1) = -1.5708
    c: Tangent(g1,g3) = -1.5708
    c: Tangent(g3,g0) = -1.5708
    c: Equal(g0,g1)
    c: Horizontal(g2)
    c: DistanceY(g-1,g1) = 7
    c: Diameter(g1) = 3
    c: Vertical(g1,g-3)
    c: Vertical(g0,g-3)
FEATURE [Part::Extrusion] Extrude005
  Base = -> Sketch006
  Dir = (0,-1,2e-16)
  DirMode = 2
  FaceMakerClass = Part::FaceMakerBullseye
  LengthFwd = 3
  LengthRev = 0
  Reversed = true
  Solid = true
  Symmetric = false
FEATURE [Sketcher::SketchObject] Sketch007
  ExternalGeometry = -> [Sketch005]
  FullyConstrained = true
  MapMode = 5
  Placement = pos=(-47.25,0,0) rot=(0.57735,-0.57735,-0.57735;2.0944rad)
  Support = -> [Cut001]
  sketch-geometry (6):
    g0: ArcOfCircle CenterX=0.75 CenterY=7 CenterZ=0 NormalX=0 NormalY=0 NormalZ=1 AngleXU=0 Radius=3.5 StartAngle=1.5708 EndAngle=4.71239
    g1: ArcOfCircle CenterX=7.75 CenterY=7 CenterZ=0 NormalX=0 NormalY=0 NormalZ=1 AngleXU=0 Radius=3.5 StartAngle=4.71239 EndAngle=7.85398
    g2: LineSegment StartX=0.75 StartY=3.5 StartZ=0 EndX=7.75 EndY=3.5 EndZ=0
    g3: LineSegment StartX=7.75 StartY=10.5 StartZ=0 EndX=0.75 EndY=10.5 EndZ=0
    g4: LineSegment StartX=-0.25 StartY=-6.5e-15 StartZ=0 EndX=0.75 EndY=3.5 EndZ=0
    g5: LineSegment StartX=7.75 StartY=3.5 StartZ=0 EndX=8.75 EndY=-6.7e-15 EndZ=0
  constraints (14):
    c: Tangent(g0,g2) = -1.5708
    c: Tangent(g2,g1) = -1.5708
    c: Tangent(g1,g3) = -1.5708
    c: Tangent(g3,g0) = -1.5708
    c: Equal(g0,g1)
    c: Horizontal(g2)
    c: DistanceY(g-1,g1) = 7
    c: Diameter(g1) = 7
    c: DistanceX(g3,g3) = 7
    c: Coincident(g4,g-3)
    c: Coincident(g4,g0)
    c: Coincident(g5,g1)
    c: Coincident(g5,g-3)
    c: Equal(g5,g4)
FEATURE [Part::Extrusion] Extrude006
  Base = -> Sketch007
  Dir = (-1,0,0)
  DirMode = 2
  FaceMakerClass = Part::FaceMakerBullseye
  LengthFwd = 3
  LengthRev = 0
  Reversed = true
  Solid = true
  Symmetric = false
FEATURE [Part::Box] Box005  label="Cube005"
  AttacherType = Attacher::AttachEngine3D
  Height = 3
  Length = 1.5
  Placement = pos=(43.75,10,7) rot=(0,0,1;0rad)
  Width = 14.7
FEATURE [Part::Chamfer] Chamfer002
  Base = -> Box005
  Edges = 4 edges r=1.49: [Edge1,Edge2,Edge3,Edge4]
FEATURE [Part::Box] Box006  label="Cube006"
  AttacherType = Attacher::AttachEngine3D
  Height = 3
  Length = 1.5
  Placement = pos=(-45.25,10,8) rot=(0,0,1;0rad)
  Width = 14.7
FEATURE [Part::Chamfer] Chamfer003
  Base = -> Box006
  Edges = 4 edges r=1.49: [Edge5,Edge6,Edge7,Edge8]
FEATURE [Part::Cut] Cut002
  Base = -> Cut001
  Tool = -> Extrude005
FEATURE [Part::Cut] Cut003
  Base = -> Cut002
  Tool = -> Extrude006
FEATURE [Part::FeaturePython] Connect  label="Main"  # WARN: FeaturePython — macro-defined, semantics opaque (R4)
  Objects = -> [Chamfer,Chamfer001,Chamfer002,Chamfer003,Cut003]
  Tolerance = 0
FEATURE [Mesh::Feature] Mesh  label="Main (Meshed)"
FEATURE [Sketcher::SketchObject] Sketch008
  ExternalGeometry = -> [Sketch007]
  FullyConstrained = true
  MapMode = 2
  Placement = pos=(-47.25,0,0) rot=(0.57735,-0.57735,-0.57735;2.0944rad)
  Support = -> [Sketch007]
  sketch-geometry (4):
    g0: ArcOfCircle CenterX=0.75 CenterY=7 CenterZ=0 NormalX=0 NormalY=0 NormalZ=1 AngleXU=0 Radius=3.2 StartAngle=1.5708 EndAngle=4.71239
    g1: ArcOfCircle CenterX=7.75 CenterY=7 CenterZ=0 NormalX=0 NormalY=0 NormalZ=1 AngleXU=0 Radius=3.2 StartAngle=4.71239 EndAngle=7.85398
    g2: LineSegment StartX=0.75 StartY=3.8 StartZ=0 EndX=7.75 EndY=3.8 EndZ=0
    g3: LineSegment StartX=7.75 StartY=10.2 StartZ=0 EndX=0.75 EndY=10.2 EndZ=0
  constraints (9):
    c: Radius(g-3) = 3.5
    c: Tangent(g0,g2) = -1.5708
    c: Tangent(g2,g1) = -1.5708
    c: Tangent(g1,g3) = -1.5708
    c: Tangent(g3,g0) = -1.5708
    c: Equal(g0,g1)
    c: Coincident(g0,g-3)
    c: Coincident(g1,g-4)
    c: Radius(g0) = 3.2
FEATURE [Part::Extrusion] Extrude007
  Base = -> Sketch008
  Dir = (-1,0,0)
  DirMode = 2
  FaceMakerClass = Part::FaceMakerBullseye
  LengthFwd = 2.4
  LengthRev = 0
  Reversed = true
  Solid = true
  Symmetric = false
FEATURE [Part::Chamfer] Chamfer004
  Base = -> Extrude007
  Edges = 1 edges: [Edge7 r1=1.5 r2=0.8]
FEATURE [Sketcher::SketchObject] Sketch009
  ExternalGeometry = -> [Sketch007]
  FullyConstrained = true
  MapMode = 2
  Placement = pos=(-47.25,0,0) rot=(0.57735,-0.57735,-0.57735;2.0944rad)
  Support = -> [Sketch007]
  sketch-geometry (4):
    g0: ArcOfCircle CenterX=0.75 CenterY=7 CenterZ=0 NormalX=0 NormalY=0 NormalZ=1 AngleXU=0 Radius=5.5 StartAngle=1.5708 EndAngle=4.71239
    g1: ArcOfCircle CenterX=7.75 CenterY=7 CenterZ=0 NormalX=0 NormalY=0 NormalZ=1 AngleXU=0 Radius=5.5 StartAngle=4.71239 EndAngle=7.85398
    g2: LineSegment StartX=0.75 StartY=1.5 StartZ=0 EndX=7.75 EndY=1.5 EndZ=0
    g3: LineSegment StartX=7.75 StartY=12.5 StartZ=0 EndX=0.75 EndY=12.5 EndZ=0
  constraints (9):
    c: Radius(g-3) = 3.5
    c: Tangent(g0,g2) = -1.5708
    c: Tangent(g2,g1) = -1.5708
    c: Tangent(g1,g3) = -1.5708
    c: Tangent(g3,g0) = -1.5708
    c: Equal(g0,g1)
    c: Coincident(g0,g-3)
    c: Coincident(g1,g-4)
    c: Radius(g0) = 5.5
FEATURE [Part::Extrusion] Extrude008
  Base = -> Sketch009
  Dir = (-1,0,0)
  DirMode = 2
  FaceMakerClass = Part::FaceMakerBullseye
  LengthFwd = 1
  LengthRev = 0
  Solid = true
  Symmetric = false
FEATURE [Part::FeaturePython] Connect001  label="Deckel_USB"  # WARN: FeaturePython — macro-defined, semantics opaque (R4)
  Objects = -> [Chamfer004,Extrude008]
  Tolerance = 0
FEATURE [Mesh::Feature] Mesh001  label="Deckel_USB (Meshed)"
  Placement = pos=(-57.5,0,48.25) rot=(0,1,0;4.71239rad)
FEATURE [Sketcher::SketchObject] Sketch010
  ExternalGeometry = -> [Sketch006]
  FullyConstrained = true
  MapMode = 2
  Placement = pos=(0,-33,0) rot=(1,0,0;1.5708rad)
  Support = -> [Sketch006]
  sketch-geometry (4):
    g0: ArcOfCircle CenterX=-11 CenterY=7 CenterZ=0 NormalX=0 NormalY=0 NormalZ=1 AngleXU=0 Radius=1.2 StartAngle=1.5708 EndAngle=4.71239
    g1: ArcOfCircle CenterX=2 CenterY=7 CenterZ=0 NormalX=0 NormalY=0 NormalZ=1 AngleXU=0 Radius=1.2 StartAngle=4.71239 EndAngle=7.85398
    g2: LineSegment StartX=-11 StartY=5.8 StartZ=0 EndX=2 EndY=5.8 EndZ=0
    g3: LineSegment StartX=2 StartY=8.2 StartZ=0 EndX=-11 EndY=8.2 EndZ=0
  constraints (9):
    c: Tangent(g0,g2) = -1.5708
    c: Tangent(g2,g1) = -1.5708
    c: Tangent(g1,g3) = -1.5708
    c: Tangent(g3,g0) = -1.5708
    c: Equal(g0,g1)
    c: Coincident(g0,g-3)
    c: Coincident(g1,g-4)
    c: Radius(g-3) = 1.5
    c: Radius(g0) = 1.2
FEATURE [Part::Extrusion] Extrude009
  Base = -> Sketch010
  Dir = (0,-1,2e-16)
  DirMode = 2
  FaceMakerClass = Part::FaceMakerBullseye
  LengthFwd = 2.4
  LengthRev = 0
  Reversed = true
  Solid = true
  Symmetric = false
FEATURE [Sketcher::SketchObject] Sketch011
  ExternalGeometry = -> [Sketch006]
  FullyConstrained = true
  MapMode = 2
  Placement = pos=(0,-33,0) rot=(1,0,0;1.5708rad)
  Support = -> [Sketch006]
  sketch-geometry (4):
    g0: ArcOfCircle CenterX=-11 CenterY=7 CenterZ=0 NormalX=0 NormalY=0 NormalZ=1 AngleXU=0 Radius=3 StartAngle=1.5708 EndAngle=4.71239
    g1: ArcOfCircle CenterX=2 CenterY=7 CenterZ=0 NormalX=0 NormalY=0 NormalZ=1 AngleXU=0 Radius=3 StartAngle=4.71239 EndAngle=7.85398
    g2: LineSegment StartX=-11 StartY=4 StartZ=0 EndX=2 EndY=4 EndZ=0
    g3: LineSegment StartX=2 StartY=10 StartZ=0 EndX=-11 EndY=10 EndZ=0
  constraints (9):
    c: Tangent(g0,g2) = -1.5708
    c: Tangent(g2,g1) = -1.5708
    c: Tangent(g1,g3) = -1.5708
    c: Tangent(g3,g0) = -1.5708
    c: Equal(g0,g1)
    c: Coincident(g0,g-3)
    c: Coincident(g1,g-4)
    c: Radius(g-3) = 1.5
    c: Radius(g0) = 3
FEATURE [Part::Extrusion] Extrude010
  Base = -> Sketch011
  Dir = (0,-1,2e-16)
  DirMode = 2
  FaceMakerClass = Part::FaceMakerBullseye
  LengthFwd = 1
  LengthRev = 0
  Solid = true
  Symmetric = false
FEATURE [Part::FeaturePython] Connect002  label="Deckel MicroSD"  # WARN: FeaturePython — macro-defined, semantics opaque (R4)
  Objects = -> [Extrude009,Extrude010]
  Tolerance = 0
FEATURE [Part::Chamfer] Chamfer005  label="Deckel MicroSD001"
  Base = -> Connect002
  Edges = 1 edges: [Edge11 r1=0.8 r2=1.5]
FEATURE [Mesh::Feature] Mesh003  label="Deckel MicroSD (Meshed)"
  Placement = pos=(0,-35.5,34) rot=(1,0,0;1.5708rad)
